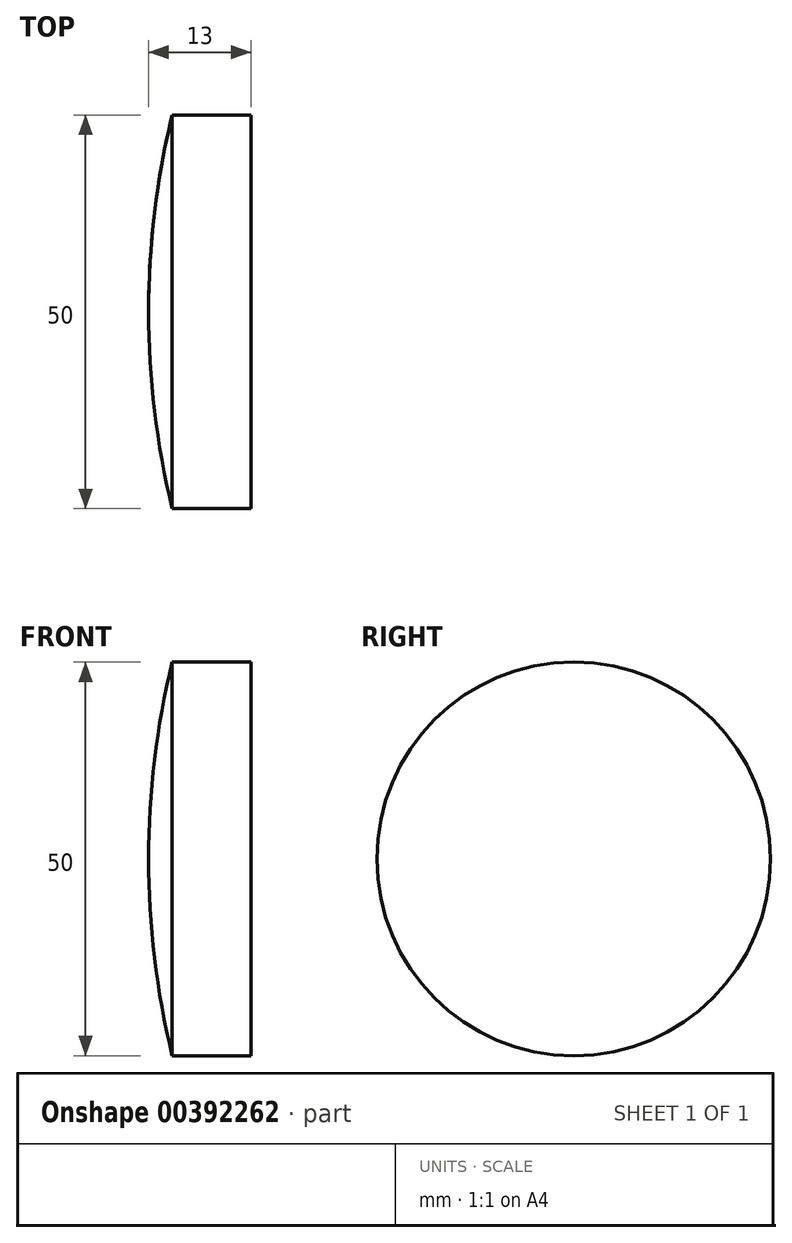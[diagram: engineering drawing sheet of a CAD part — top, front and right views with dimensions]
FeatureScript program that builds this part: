
annotation { "Feature Type Name" : "Feature", "Feature Type Description" : "" }
export const myFeature = defineFeature(function(context is Context, id is Id, definition is map)
    precondition{}
    {
        {
            var Q0;
            Q0=qCreatedBy(makeId("Right.planeOp"),FACE);
            var sketch = newSketch(context, id + "F0", { "sketchPlane" : qUnion([Q0])});
            skCircle(sketch, "E0", {"center": v(0, 0) * mm, "radius": 25 * mm});
            skSolve(sketch);
        }
        {
            var Q0;
            Q0 = qSketchRegion(id + "F0", true);
            extrude(context, id + "F1", {"entities" : qUnion([Q0]), "depth" : 10 * mm, "offsetDistance" : 25 * mm});
        }
        {
            var Q0;
            Q0=qCreatedBy(makeId("Top.planeOp"),FACE);
            var sketch = newSketch(context, id + "F2", { "sketchPlane" : qUnion([Q0])});
            skLineSegment(sketch, "E1.0", {"start": v(0, 25) * mm, "end": v(0, -25) * mm});
            skArc(sketch, "E2", {"start": v(-3, 0) * mm, "mid": v(-2.25, -12.59) * mm, "end": v(0, -25) * mm});
            skLineSegment(sketch, "E3", {"start": v(0, 0) * mm, "end": v(-3, 0) * mm});
            skSolve(sketch);
        }
        {
            var Q0;
            Q0 = qSketchRegion(id + "F2", true);
            var Q1;
            Q1=sQuery(id+"F2.wireOp",EDGE,"E3");
            revolve(context, id + "F3", {"operationType" : NewBodyOperationType.ADD, "entities" : qUnion([Q0]), "axis" : qUnion([Q1]), "revolveType" : RevolveType.FULL});
        }
    });
